# Revit family: Legrand-Industrial_Enclosures-Metal-Altis_Cabinets-D_600
name_source: partatom
category: Equipement électrique
units: mm (PartAtom-declared; Revit-internal decimal feet)

## family parameters
Basée sur le plan de construction = Non
Configuration du panneau = Deux colonnes, circuits au sein
Cote de connecteur circulaire = Utiliser le diamètre
Couper avec des vides une fois chargée = Non
Numéro OmniClass = 23.80.30.11.17
Partagée = Non
Point de calcul de pièce = Non
Titre OmniClass = Distribution Boards and Control Panels
Toujours verticalement = Oui
Type d'élément = Tableau de raccordement

## types (16) — shared parameters
ETIM Class 6.0 = EC000261
Fabricant = Legrand
General Conditions of Use = https://export.legrand.com
IK = 10
IP = 55
Image du type = Altis_047101_pw_133028_pz_48.jpg
Material = Polyester
RAL = 7035
URL = www.legrand.fr
depth = 600 mm
error double plinth height = Non
no plinth = Oui
plinth height 100 width 1000 = Non
plinth height 100 width 1200 = Non
plinth height 100 width 1600 = Non
plinth height 100 width 400 = Non
plinth height 100 width 600 = Non
plinth height 100 width 800 = Non
plinth height 200 width 1000 = Non
plinth height 200 width 1200 = Non
plinth height 200 width 1600 = Non
plinth height 200 width 400 = Non
plinth height 200 width 600 = Non
plinth height 200 width 800 = Non
socle 100mm = Non
socle 200mm = Non
zero-valued in all types: Elévation par défaut, plinth height

## per-type parameters (varying)
| type | Cabinet 047240 | Cabinet 047241 | Cabinet 047244 | Cabinet 047245 | Cabinet 047246 | Cabinet 047247 | Cabinet 047248 | Cabinet 047249 | Cabinet 047250 | Cabinet 047251 | Cabinet 047252 | Cabinet 047253 | Cabinet 047254 | Cabinet 047255 | Cabinet 047256 | Cabinet 047257 | Depth installation zone | Description | Width installation zone | distance to installation zone | height | weight | width |
| Industrial enclosures - Altis - Assemblable - Metal - Depth 600mm - Height 1200mm - Width  600mm | Oui | Non | Non | Non | Non | Non | Non | Non | Non | Non | Non | Non | Non | Non | Non | Non | 1200 mm | Ref 047240 - Enveloppe industrielle - Altis - Assemblable - Métal - Profondeur 600mm | 2200 mm | 600 mm | 1223 mm  [stored 4.01247 ft] | 67.60 kg | 600 mm |
| Industrial enclosures - Altis - Assemblable - Metal - Depth 600mm - Height 1200mm - Width  800mm | Non | Oui | Non | Non | Non | Non | Non | Non | Non | Non | Non | Non | Non | Non | Non | Non | 1400 mm  [stored 4.59318 ft] | Ref 047241 - Enveloppe industrielle - Altis - Assemblable - Métal - Profondeur 600mm | 2400 mm | 800 mm  [stored 2.62467 ft] | 1223 mm  [stored 4.01247 ft] | 83.00 kg | 800 mm  [stored 2.62467 ft] |
| Industrial enclosures - Altis - Assemblable - Metal - Depth 600mm - Height 1800mm - Width  400mm | Non | Non | Non | Non | Oui | Non | Non | Non | Non | Non | Non | Non | Non | Non | Non | Non | 1000 mm  [stored 3.28084 ft] | Ref 047246 - Enveloppe industrielle - Altis - Assemblable - Métal - Profondeur 600mm | 2000 mm  [stored 6.56168 ft] | 400 mm  [stored 1.31234 ft] | 1823 mm  [stored 5.98097 ft] | 104.00 kg | 400 mm  [stored 1.31234 ft] |
| Industrial enclosures - Altis - Assemblable - Metal - Depth 600mm - Height 1600mm - Width  600mm | Non | Non | Non | Non | Non | Oui | Non | Non | Non | Non | Non | Non | Non | Non | Non | Non | 1200 mm | Ref 047247 - Enveloppe industrielle - Altis - Assemblable - Métal - Profondeur 600mm | 2200 mm | 600 mm | 1823 mm  [stored 5.98097 ft] | 79.30 kg | 600 mm |
| Industrial enclosures - Altis - Assemblable - Metal - Depth 600mm - Height 1800mm - Width  800mm | Non | Non | Non | Non | Non | Non | Oui | Non | Non | Non | Non | Non | Non | Non | Non | Non | 1400 mm  [stored 4.59318 ft] | Ref 047248 - Enveloppe industrielle - Altis - Assemblable - Métal - Profondeur 600mm | 2400 mm | 800 mm  [stored 2.62467 ft] | 1823 mm  [stored 5.98097 ft] | 93.10 kg | 800 mm  [stored 2.62467 ft] |
| Industrial enclosures - Altis - Assemblable - Metal - Depth 600mm - Height 1800mm - Width 1000mm - With door recentring | Non | Non | Non | Non | Non | Non | Non | Oui | Non | Non | Non | Non | Non | Non | Non | Non | 1600 mm  [stored 5.24934 ft] | Ref 047249 - Enveloppe industrielle - Altis - Assemblable - Métal - Profondeur 600mm | 2600 mm  [stored 8.53018 ft] | 1000 mm  [stored 3.28084 ft] | 1823 mm  [stored 5.98097 ft] | 106.40 kg | 1000 mm  [stored 3.28084 ft] |
| Industrial enclosures - Altis - Assemblable - Metal - Depth 600mm - Height 1800mm - Width  1200mm | Non | Non | Non | Non | Non | Non | Non | Non | Oui | Non | Non | Non | Non | Non | Non | Non | 1800 mm  [stored 5.90551 ft] | Ref 047250 - Enveloppe industrielle - Altis - Assemblable - Métal - Profondeur 600mm | 2800 mm  [stored 9.18635 ft] | 1200 mm | 1823 mm  [stored 5.98097 ft] | 137.40 kg | 1200 mm |
| Industrial enclosures - Altis - Assemblable - Metal - Depth 600mm - Height 2000mm - Width  400mm | Non | Non | Non | Non | Non | Non | Non | Non | Non | Oui | Non | Non | Non | Non | Non | Non | 1000 mm  [stored 3.28084 ft] | Ref 047251 - Enveloppe industrielle - Altis - Assemblable - Métal - Profondeur 600mm | 2000 mm  [stored 6.56168 ft] | 400 mm  [stored 1.31234 ft] | 2023 mm  [stored 6.63714 ft] | 60.10 kg | 400 mm  [stored 1.31234 ft] |
| Industrial enclosures - Altis - Assemblable - Metal - Depth 600mm - Height 2000mm - Width  600mm | Non | Non | Non | Non | Non | Non | Non | Non | Non | Non | Oui | Non | Non | Non | Non | Non | 1200 mm | Ref 047252 - Enveloppe industrielle - Altis - Assemblable - Métal - Profondeur 600mm | 2200 mm | 600 mm | 2023 mm  [stored 6.63714 ft] | 83.20 kg | 600 mm |
| Industrial enclosures - Altis - Assemblable - Metal - Depth 600mm - Height 2000mm - Width  800mm | Non | Non | Non | Non | Non | Non | Non | Non | Non | Non | Non | Oui | Non | Non | Non | Non | 1400 mm  [stored 4.59318 ft] | Ref 047253 - Enveloppe industrielle - Altis - Assemblable - Métal - Profondeur 600mm | 2400 mm | 800 mm  [stored 2.62467 ft] | 2023 mm  [stored 6.63714 ft] | 98.00 kg | 800 mm  [stored 2.62467 ft] |
| Industrial enclosures - Altis - Assemblable - Metal - Depth 600mm - Height 2000mm - Width 1000mm - With door recentring | Non | Non | Non | Non | Non | Non | Non | Non | Non | Non | Non | Non | Oui | Non | Non | Non | 1600 mm  [stored 5.24934 ft] | Ref 047254 - Enveloppe industrielle - Altis - Assemblable - Métal - Profondeur 600mm | 2600 mm  [stored 8.53018 ft] | 1000 mm  [stored 3.28084 ft] | 2023 mm  [stored 6.63714 ft] | 112.30 kg | 1000 mm  [stored 3.28084 ft] |
| Industrial enclosures - Altis - Assemblable - Metal - Depth 600mm - Height 2000mm - Width  1000mm | Non | Non | Non | Non | Non | Non | Non | Non | Non | Non | Non | Non | Non | Oui | Non | Non | 1600 mm  [stored 5.24934 ft] | Ref 047255 - Enveloppe industrielle - Altis - Assemblable - Métal - Profondeur 600mm | 2600 mm  [stored 8.53018 ft] | 1000 mm  [stored 3.28084 ft] | 2023 mm  [stored 6.63714 ft] | 117.00 kg | 1000 mm  [stored 3.28084 ft] |
| Industrial enclosures - Altis - Assemblable - Metal - Depth 600mm - Height 2000mm - Width  1200mm | Non | Non | Non | Non | Non | Non | Non | Non | Non | Non | Non | Non | Non | Non | Oui | Non | 1800 mm  [stored 5.90551 ft] | Ref 047256 - Enveloppe industrielle - Altis - Assemblable - Métal - Profondeur 600mm | 2800 mm  [stored 9.18635 ft] | 1200 mm | 2023 mm  [stored 6.63714 ft] | 144.30 kg | 1200 mm |
| Industrial enclosures - Altis - Assemblable - Metal - Depth 600mm - Height 2000mm - Width  1600mm | Non | Non | Non | Non | Non | Non | Non | Non | Non | Non | Non | Non | Non | Non | Non | Oui | 2200 mm | Ref 047257 - Enveloppe industrielle - Altis - Assemblable - Métal - Profondeur 600mm | 3200 mm  [stored 10.4987 ft] | 1600 mm  [stored 5.24934 ft] | 2023 mm  [stored 6.63714 ft] | 150.50 kg | 1600 mm  [stored 5.24934 ft] |
| Industrial enclosures - Altis - Assemblable - Metal - Depth 600mm - Height 1800mm - Width  600mm | Non | Non | Oui | Non | Non | Non | Non | Non | Non | Non | Non | Non | Non | Non | Non | Non | 1200 mm | Ref 047244 - Enveloppe industrielle - Altis - Assemblable - Métal - Profondeur 600mm | 2200 mm | 600 mm | 1623 mm  [stored 5.3248 ft] | 148.00 kg | 600 mm |
| Industrial enclosures - Altis - Assemblable - Metal - Depth 600mm - Height 1600mm - Width  800mm | Non | Non | Non | Oui | Non | Non | Non | Non | Non | Non | Non | Non | Non | Non | Non | Non | 1400 mm  [stored 4.59318 ft] | Ref 047245 - Enveloppe industrielle - Altis - Assemblable - Métal - Profondeur 600mm | 2400 mm | 800 mm  [stored 2.62467 ft] | 1623 mm  [stored 5.3248 ft] | 88.20 kg | 800 mm  [stored 2.62467 ft] |

note: [stored X ft] marks values corroborated as IEEE doubles in the binary element streams (Revit-internal decimal feet)
